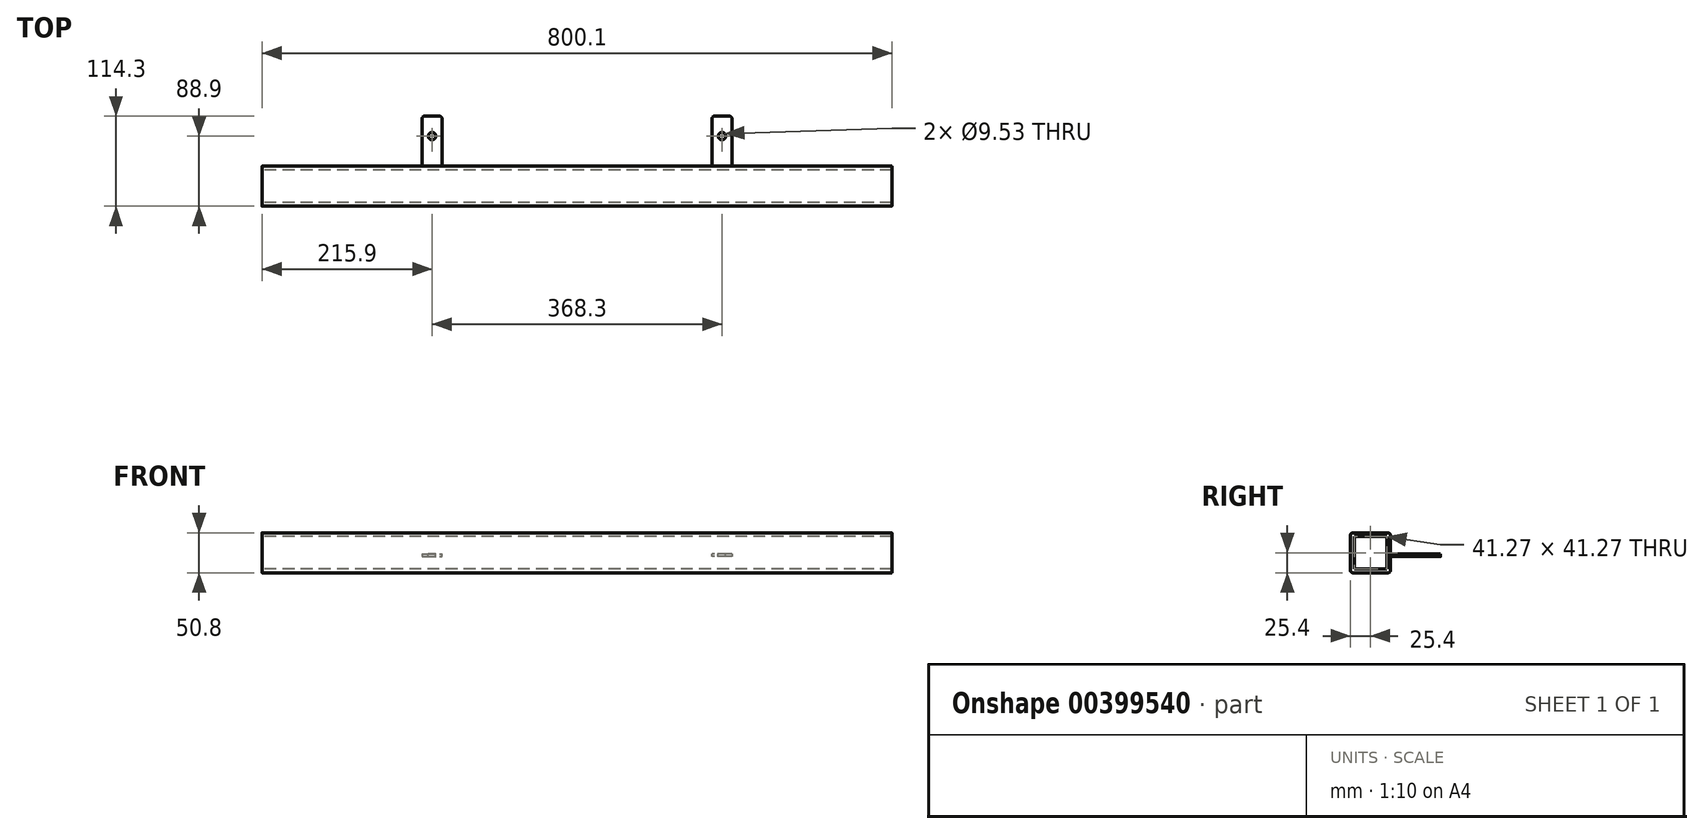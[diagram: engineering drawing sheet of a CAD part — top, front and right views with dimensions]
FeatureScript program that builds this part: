
annotation { "Feature Type Name" : "Feature", "Feature Type Description" : "" }
export const myFeature = defineFeature(function(context is Context, id is Id, definition is map)
    precondition{}
    {
        {
            var Q0;
            Q0=qCreatedBy(makeId("Right.planeOp"),FACE);
            var sketch = newSketch(context, id + "F0", { "sketchPlane" : qUnion([Q0])});
            skLineSegment(sketch, "E0.bottom", {"start": v(22.23, 25.4) * mm, "end": v(-22.23, 25.4) * mm});
            skLineSegment(sketch, "E0.top", {"start": v(22.23, -25.4) * mm, "end": v(-22.23, -25.4) * mm});
            skLineSegment(sketch, "E0.left", {"start": v(25.4, 22.23) * mm, "end": v(25.4, -22.23) * mm});
            skLineSegment(sketch, "E0.right", {"start": v(-25.4, 22.23) * mm, "end": v(-25.4, -22.23) * mm});
            skPoint(sketch, "E0.middle", {"position": v(0, 0) * mm});
            skPoint(sketch, "E1.visualSharp", {"position": v(-25.4, 25.4) * mm});
            skArc(sketch, "E1.filletArc", {"start": v(-22.23, 25.4) * mm, "mid": v(-24.47, 24.47) * mm, "end": v(-25.4, 22.23) * mm});
            skPoint(sketch, "E2.visualSharp", {"position": v(25.4, 25.4) * mm});
            skArc(sketch, "E2.filletArc", {"start": v(25.4, 22.23) * mm, "mid": v(24.47, 24.47) * mm, "end": v(22.23, 25.4) * mm});
            skPoint(sketch, "E3.visualSharp", {"position": v(25.4, -25.4) * mm});
            skArc(sketch, "E3.filletArc", {"start": v(22.23, -25.4) * mm, "mid": v(24.47, -24.47) * mm, "end": v(25.4, -22.23) * mm});
            skPoint(sketch, "E4.visualSharp", {"position": v(-25.4, -25.4) * mm});
            skArc(sketch, "E4.filletArc", {"start": v(-25.4, -22.23) * mm, "mid": v(-24.47, -24.47) * mm, "end": v(-22.23, -25.4) * mm});
            skLineSegment(sketch, "E5.0", {"start": v(-20.64, 20.64) * mm, "end": v(-20.64, -20.64) * mm});
            skLineSegment(sketch, "E5.1", {"start": v(20.64, 20.64) * mm, "end": v(-20.64, 20.64) * mm});
            skLineSegment(sketch, "E5.2", {"start": v(20.64, 20.64) * mm, "end": v(20.64, -20.64) * mm});
            skLineSegment(sketch, "E5.3", {"start": v(20.64, -20.64) * mm, "end": v(-20.64, -20.64) * mm});
            skSolve(sketch);
        }
        {
            var Q0;
            Q0=makeQuery(id+"F0.imprint","IMPRINT",FACE,{"disambiguationData":[TD([[makeQuery(id+"F0.imprint","IMPRINT",EDGE,{"derivedFrom":sQuery(id+"F0.wireOp",EDGE,"E0.bottom")}),1.0]])]});
            extrude(context, id + "F1", {"entities" : qUnion([Q0]), "endBound" : BoundingType.SYMMETRIC, "depth" : 800.1 * mm});
        }
        {
            var Q0;
            Q0=makeQuery(id+"F1.opExtrude","SWEPT_FACE",FACE,{"disambiguationData":[OSD([sQuery(id+"F0.wireOp",EDGE,"E0.left")])]});
            var sketch = newSketch(context, id + "F2", { "sketchPlane" : qUnion([Q0])});
            skLineSegment(sketch, "E6", {"start": v(0, 22.23) * mm, "end": v(0, -22.23) * mm, "construction": true});
            skLineSegment(sketch, "E7.0", {"start": v(-31.75, 22.23) * mm, "end": v(-31.75, -22.23) * mm, "construction": true});
            skLineSegment(sketch, "E8.0", {"start": v(-336.55, 22.23) * mm, "end": v(-336.55, -22.23) * mm, "construction": true});
            skLineSegment(sketch, "E9", {"start": v(-31.75, 0) * mm, "end": v(-336.55, 0) * mm, "construction": true});
            skLineSegment(sketch, "E10", {"start": v(-184.15, -22.23) * mm, "end": v(-184.15, 22.23) * mm, "construction": true});
            skPoint(sketch, "E10.startSnap0", {"position": v(-184.15, 0) * mm});
            skLineSegment(sketch, "E11.0", {"start": v(-184.15, -22.22) * mm, "end": v(-184.15, -1.52) * mm, "construction": true});
            skLineSegment(sketch, "E12", {"start": v(-196.85, -1.52) * mm, "end": v(-171.45, -1.52) * mm});
            skLineSegment(sketch, "E13", {"start": v(-196.85, -1.52) * mm, "end": v(-196.85, -4.7) * mm});
            skLineSegment(sketch, "E14", {"start": v(-196.85, -4.7) * mm, "end": v(-171.45, -4.7) * mm});
            skLineSegment(sketch, "E15", {"start": v(-171.45, -4.7) * mm, "end": v(-171.45, -1.52) * mm});
            skLineSegment(sketch, "E16.MirrorCS", {"start": v(171.45, -4.7) * mm, "end": v(171.45, -1.52) * mm});
            skLineSegment(sketch, "E17.MirrorCS", {"start": v(196.85, -1.52) * mm, "end": v(196.85, -4.7) * mm});
            skLineSegment(sketch, "E18.MirrorCS", {"start": v(196.85, -4.7) * mm, "end": v(171.45, -4.7) * mm});
            skLineSegment(sketch, "E19.MirrorCS", {"start": v(196.85, -1.52) * mm, "end": v(171.45, -1.52) * mm});
            skPoint(sketch, "E20.MirrorP", {"position": v(184.15, 0) * mm});
            skLineSegment(sketch, "E21.MirrorCS", {"start": v(336.55, 22.23) * mm, "end": v(336.55, -22.23) * mm, "construction": true});
            skLineSegment(sketch, "E22.MirrorCS", {"start": v(31.75, 0) * mm, "end": v(336.55, 0) * mm, "construction": true});
            skLineSegment(sketch, "E23.MirrorCS", {"start": v(184.15, -22.22) * mm, "end": v(184.15, -1.52) * mm, "construction": true});
            skLineSegment(sketch, "E24.MirrorCS", {"start": v(184.15, -22.23) * mm, "end": v(184.15, 22.23) * mm, "construction": true});
            skLineSegment(sketch, "E25.MirrorCS", {"start": v(31.75, 22.23) * mm, "end": v(31.75, -22.23) * mm, "construction": true});
            skLineSegment(sketch, "E26.MirrorCS", {"start": v(58.06, -22.23) * mm, "end": v(58.06, 22.23) * mm, "construction": true});
            skPoint(sketch, "E27", {"position": v(-184.15, -1.52) * mm});
            skSolve(sketch);
        }
        {
            var Q0;
            Q0=makeQuery(id+"F2.imprint","IMPRINT",FACE,{"disambiguationData":[TD([[makeQuery(id+"F2.imprint","IMPRINT",EDGE,{"derivedFrom":sQuery(id+"F2.wireOp",EDGE,"E12")}),-1.0]])]});
            var Q1;
            Q1=makeQuery(id+"F2.imprint","IMPRINT",FACE,{"disambiguationData":[TD([[makeQuery(id+"F2.imprint","IMPRINT",EDGE,{"derivedFrom":sQuery(id+"F2.wireOp",EDGE,"befbe1bb-d01f-48cb-91fc-e482287dd12f0.MirrorCS")}),-1.0]])]});
            var Q2;
            Q2=makeQuery(id+"F2.imprint","IMPRINT",FACE,{"disambiguationData":[TD([[makeQuery(id+"F2.imprint","IMPRINT",EDGE,{"derivedFrom":sQuery(id+"F2.wireOp",EDGE,"245204af-2cdf-4e48-8b8f-9375b151ac541.MirrorCS")}),1.0]])]});
            var Q3;
            Q3=makeQuery(id+"F2.imprint","IMPRINT",FACE,{"disambiguationData":[TD([[makeQuery(id+"F2.imprint","IMPRINT",EDGE,{"derivedFrom":sQuery(id+"F2.wireOp",EDGE,"E16.MirrorCS")}),-1.0]])]});
            extrude(context, id + "F3", {"entities" : qUnion([Q0, Q1, Q2, Q3]), "operationType" : NewBodyOperationType.ADD, "depth" : 63.5 * mm});
        }
        {
            var Q0;
            Q0=makeQuery(id+"F3.opExtrude","CAP_EDGE",EDGE,{"disambiguationData":[OSD([sQuery(id+"F2.wireOp",EDGE,"E13")])],"isStart":false});
            var Q1;
            Q1=makeQuery(id+"F3.opExtrude","CAP_EDGE",EDGE,{"disambiguationData":[OSD([sQuery(id+"F2.wireOp",EDGE,"E15")])],"isStart":false});
            var Q2;
            Q2=makeQuery(id+"F3.opExtrude","CAP_EDGE",EDGE,{"disambiguationData":[OSD([sQuery(id+"F2.wireOp",EDGE,"befbe1bb-d01f-48cb-91fc-e482287dd12f2.MirrorCS")])],"isStart":false});
            var Q3;
            Q3=makeQuery(id+"F3.opExtrude","CAP_EDGE",EDGE,{"disambiguationData":[OSD([sQuery(id+"F2.wireOp",EDGE,"befbe1bb-d01f-48cb-91fc-e482287dd12f0.MirrorCS")])],"isStart":false});
            var Q4;
            Q4=makeQuery(id+"F3.opExtrude","CAP_EDGE",EDGE,{"disambiguationData":[OSD([sQuery(id+"F2.wireOp",EDGE,"245204af-2cdf-4e48-8b8f-9375b151ac541.MirrorCS")])],"isStart":false});
            var Q5;
            Q5=makeQuery(id+"F3.opExtrude","CAP_EDGE",EDGE,{"disambiguationData":[OSD([sQuery(id+"F2.wireOp",EDGE,"245204af-2cdf-4e48-8b8f-9375b151ac542.MirrorCS")])],"isStart":false});
            var Q6;
            Q6=makeQuery(id+"F3.opExtrude","CAP_EDGE",EDGE,{"disambiguationData":[OSD([sQuery(id+"F2.wireOp",EDGE,"E16.MirrorCS")])],"isStart":false});
            var Q7;
            Q7=makeQuery(id+"F3.opExtrude","CAP_EDGE",EDGE,{"disambiguationData":[OSD([sQuery(id+"F2.wireOp",EDGE,"E17.MirrorCS")])],"isStart":false});
            fillet(context, id + "F4", {"entities" : qUnion([Q0, Q1, Q2, Q3, Q4, Q5, Q6, Q7]), "radius" : 3.17 * mm, "tangentPropagation" : true, "allowEdgeOverflow" : false});
        }
        {
            var Q0;
            Q0=makeQuery(id+"F3.opExtrude","SWEPT_FACE",FACE,{"disambiguationData":[OSD([sQuery(id+"F2.wireOp",EDGE,"befbe1bb-d01f-48cb-91fc-e482287dd12f1.MirrorCS")])]});
            var sketch = newSketch(context, id + "F5", { "sketchPlane" : qUnion([Q0])});
            skLineSegment(sketch, "E28", {"start": v(142.87, 88.9) * mm, "end": v(142.87, 63.5) * mm});
            skSolve(sketch);
        }
        {
            var Q0;
            Q0=makeQuery(id+"F3.opExtrude","SWEPT_FACE",FACE,{"disambiguationData":[OSD([sQuery(id+"F2.wireOp",EDGE,"E19.MirrorCS")])]});
            var sketch = newSketch(context, id + "F6", { "sketchPlane" : qUnion([Q0])});
            skLineSegment(sketch, "E29", {"start": v(-184.15, 88.9) * mm, "end": v(-184.15, 63.5) * mm});
            skSolve(sketch);
        }
        {
            var Q0;
            Q0=makeQuery(id+"F3.opExtrude","SWEPT_FACE",FACE,{"disambiguationData":[OSD([sQuery(id+"F2.wireOp",EDGE,"E12")])]});
            var sketch = newSketch(context, id + "F7", { "sketchPlane" : qUnion([Q0])});
            skLineSegment(sketch, "E30", {"start": v(184.15, 88.9) * mm, "end": v(184.15, 63.5) * mm});
            skSolve(sketch);
        }
        {
            var Q0;
            Q0=makeQuery(id+"F3.opExtrude","SWEPT_FACE",FACE,{"disambiguationData":[OSD([sQuery(id+"F2.wireOp",EDGE,"245204af-2cdf-4e48-8b8f-9375b151ac544.MirrorCS")])]});
            var sketch = newSketch(context, id + "F8", { "sketchPlane" : qUnion([Q0])});
            skLineSegment(sketch, "E31", {"start": v(-142.87, 88.9) * mm, "end": v(-142.87, 63.5) * mm});
            skSolve(sketch);
        }
        {
            var Q0;
            Q0=sQuery(id+"F5.wireOp",VERTEX,"RfbAE9f0-sgwl-5tex-rEcf-8U1bwM1ILnGr.end");
            var Q1;
            Q1=sQuery(id+"F5.wireOp",VERTEX,"5qpLVkBl-V1lU-lDmT-DBrx-aJekFXyM72kz.end");
            var Q2;
            Q2=sQuery(id+"F8.wireOp",VERTEX,"aSFsBNaK-4hI9-qLBb-AoAY-WHHGJ4j7iWG9.end");
            var Q3;
            Q3=sQuery(id+"F6.wireOp",VERTEX,"IZp5sdTc-TNsN-Rvwu-ysIC-KQbioU6J6yvI.end");
            var Q4;
            Q4=sQuery(id+"F7.wireOp",VERTEX,"E30.end");
            var Q5;
            Q5=sQuery(id+"F5.wireOp",VERTEX,"E28.end");
            var Q6;
            Q6=sQuery(id+"F8.wireOp",VERTEX,"E31.end");
            var Q7;
            Q7=sQuery(id+"F6.wireOp",VERTEX,"E29.end");
            var Q8;
            Q8=makeQuery(id+"F1.opExtrude","SWEPT_BODY",BODY,{"disambiguationData":[OSD([sQuery(id+"F0.wireOp",EDGE,"E0.bottom"),sQuery(id+"F0.wireOp",EDGE,"E0.top"),sQuery(id+"F0.wireOp",EDGE,"E0.left"),sQuery(id+"F0.wireOp",EDGE,"E0.right"),sQuery(id+"F0.wireOp",EDGE,"E1.filletArc"),sQuery(id+"F0.wireOp",EDGE,"E2.filletArc"),sQuery(id+"F0.wireOp",EDGE,"E3.filletArc"),sQuery(id+"F0.wireOp",EDGE,"E4.filletArc"),sQuery(id+"F0.wireOp",EDGE,"E5.0"),sQuery(id+"F0.wireOp",EDGE,"E5.1"),sQuery(id+"F0.wireOp",EDGE,"E5.2"),sQuery(id+"F0.wireOp",EDGE,"E5.3")])]});
            hole(context, id + "F9", {"style" : HoleStyle.SIMPLE, "endStyle" : HoleEndStyle.THROUGH, "holeDiameter" : 9.52 * mm, "locations" : qUnion([Q0, Q1, Q2, Q3, Q4, Q5, Q6, Q7]), "scope" : qUnion([Q8]), "isTappedThrough" : true});
        }
    });
